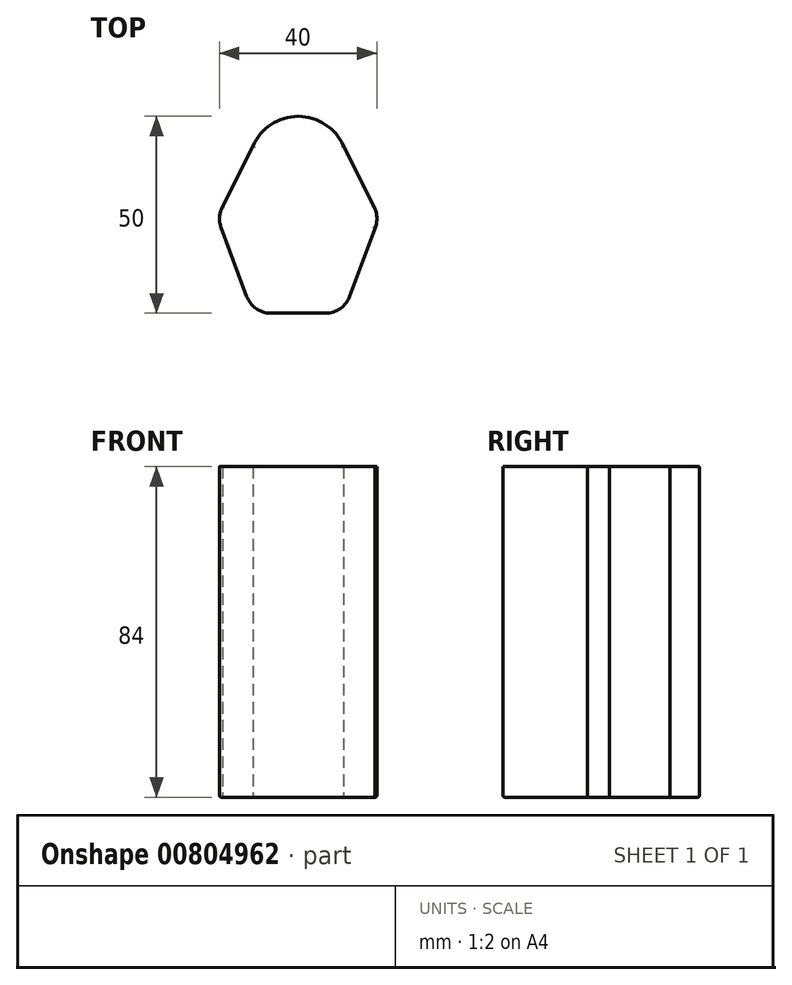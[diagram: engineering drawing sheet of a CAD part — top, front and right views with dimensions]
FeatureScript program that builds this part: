
annotation { "Feature Type Name" : "Feature", "Feature Type Description" : "" }
export const myFeature = defineFeature(function(context is Context, id is Id, definition is map)
    precondition{}
    {
        {
            var Q0;
            Q0=qCreatedBy(makeId("Top.planeOp"),FACE);
            var sketch = newSketch(context, id + "F0", { "sketchPlane" : qUnion([Q0])});
            skArc(sketch, "E0", {"start": v(11.49, 20.22) * mm, "mid": v(0, 27.79) * mm, "end": v(-11.48, 20.22) * mm});
            skLineSegment(sketch, "E1", {"start": v(-7, -22.21) * mm, "end": v(7, -22.21) * mm});
            skArc(sketch, "E2", {"start": v(-19.2, 4.91) * mm, "mid": v(-19.98, 2.23) * mm, "end": v(-19.57, -0.53) * mm});
            skArc(sketch, "E3", {"start": v(19.51, -0.69) * mm, "mid": v(20, 2.15) * mm, "end": v(19.2, 4.91) * mm});
            skArc(sketch, "E4", {"start": v(-13.1, -17.98) * mm, "mid": v(-10.7, -21.05) * mm, "end": v(-7, -22.21) * mm});
            skArc(sketch, "E5", {"start": v(7, -22.21) * mm, "mid": v(10.71, -21.05) * mm, "end": v(13.1, -17.97) * mm});
            skLineSegment(sketch, "E6", {"start": v(-19.57, -0.53) * mm, "end": v(-13.1, -17.98) * mm});
            skLineSegment(sketch, "E7", {"start": v(13.1, -17.97) * mm, "end": v(19.51, -0.69) * mm});
            skLineSegment(sketch, "E8", {"start": v(-19.2, 4.91) * mm, "end": v(-11.48, 20.22) * mm});
            skLineSegment(sketch, "E9", {"start": v(11.49, 20.22) * mm, "end": v(19.2, 4.91) * mm});
            skPoint(sketch, "E10.orphan", {"position": v(-7, 15.29) * mm});
            skPoint(sketch, "E11.start.orphan", {"position": v(0, 27.79) * mm});
            skPoint(sketch, "E12.orphan", {"position": v(7, 15.29) * mm});
            skSolve(sketch);
        }
        {
            var Q0;
            Q0 = qSketchRegion(id + "F0", true);
            extrude(context, id + "F1", {"entities" : qUnion([Q0]), "depth" : 84 * mm, "offsetDistance" : 25 * mm});
        }
        {
            var Q0;
            Q0=makeQuery(id+"F1.opExtrude","CAP_EDGE",EDGE,{"disambiguationData":[OSD([sQuery(id+"F0.wireOp",EDGE,"E0")])],"isStart":true});
            var Q1;
            Q1=makeQuery(id+"F1.opExtrude","CAP_EDGE",EDGE,{"disambiguationData":[OSD([sQuery(id+"F0.wireOp",EDGE,"E8")])],"isStart":true});
            var Q2;
            Q2=makeQuery(id+"F1.opExtrude","CAP_EDGE",EDGE,{"disambiguationData":[OSD([sQuery(id+"F0.wireOp",EDGE,"E2")])],"isStart":true});
            var Q3;
            Q3=makeQuery(id+"F1.opExtrude","CAP_EDGE",EDGE,{"disambiguationData":[OSD([sQuery(id+"F0.wireOp",EDGE,"E6")])],"isStart":true});
            var Q4;
            Q4=makeQuery(id+"F1.opExtrude","CAP_EDGE",EDGE,{"disambiguationData":[OSD([sQuery(id+"F0.wireOp",EDGE,"E4")])],"isStart":true});
            var Q5;
            Q5=makeQuery(id+"F1.opExtrude","CAP_EDGE",EDGE,{"disambiguationData":[OSD([sQuery(id+"F0.wireOp",EDGE,"E1")])],"isStart":true});
            var Q6;
            Q6=makeQuery(id+"F1.opExtrude","CAP_EDGE",EDGE,{"disambiguationData":[OSD([sQuery(id+"F0.wireOp",EDGE,"E5")])],"isStart":true});
            var Q7;
            Q7=makeQuery(id+"F1.opExtrude","CAP_EDGE",EDGE,{"disambiguationData":[OSD([sQuery(id+"F0.wireOp",EDGE,"E7")])],"isStart":true});
            var Q8;
            Q8=makeQuery(id+"F1.opExtrude","CAP_EDGE",EDGE,{"disambiguationData":[OSD([sQuery(id+"F0.wireOp",EDGE,"E3")])],"isStart":true});
            var Q9;
            Q9=makeQuery(id+"F1.opExtrude","CAP_EDGE",EDGE,{"disambiguationData":[OSD([sQuery(id+"F0.wireOp",EDGE,"E9")])],"isStart":true});
            fillet(context, id + "F2", {"entities" : qUnion([Q0, Q1, Q2, Q3, Q4, Q5, Q6, Q7, Q8, Q9]), "radius" : .5 * mm, "tangentPropagation" : true, "allowEdgeOverflow" : false});
        }
    });
